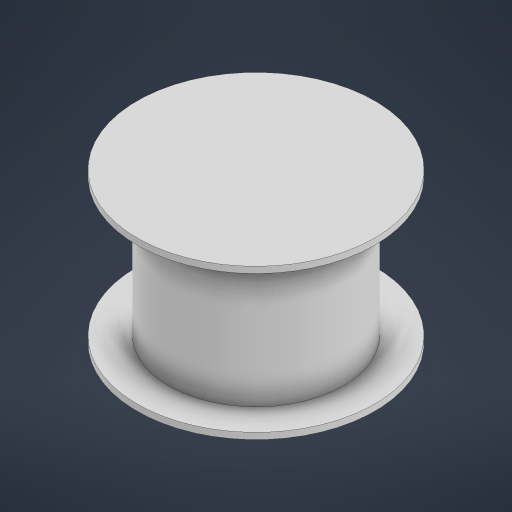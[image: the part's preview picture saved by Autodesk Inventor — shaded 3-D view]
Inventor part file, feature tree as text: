
AUTODESK INVENTOR PART (.ipt)
format: ipt  version: 2023 (Build 270158000, 158)  size: 193,024 bytes
history: native  units: in
note: dims shown in document units (in); Inventor stores cm internally (conversion verified against a paired STEP export)
features: extrude x3, sketch x3
ambient origin geometry x8: Origin, YZ Plane, XZ Plane, XY Plane, X Axis, Y Axis, Z Axis, Center Point
bodies: Solid1 (feature_tree)
feature tree (6):
  extrude  "Extrusion1"  Depth=0.9449in
  sketch  "Sketch3"  dims[d4=0.0394in d5=0.0in d7=1.1024in]
  extrude  "Extrusion3"  Depth=0.0394in
  sketch  "Sketch5"  dims[d10=0.8661in d11=0.0in d14=0.0394in d15=0.0in]
  extrude  "Extrusion5"  Depth=0.0394in TaperAngle=0.0deg
  sketch  "Sketch1"  dims[d1=1.4961in d3=0.9449in]
